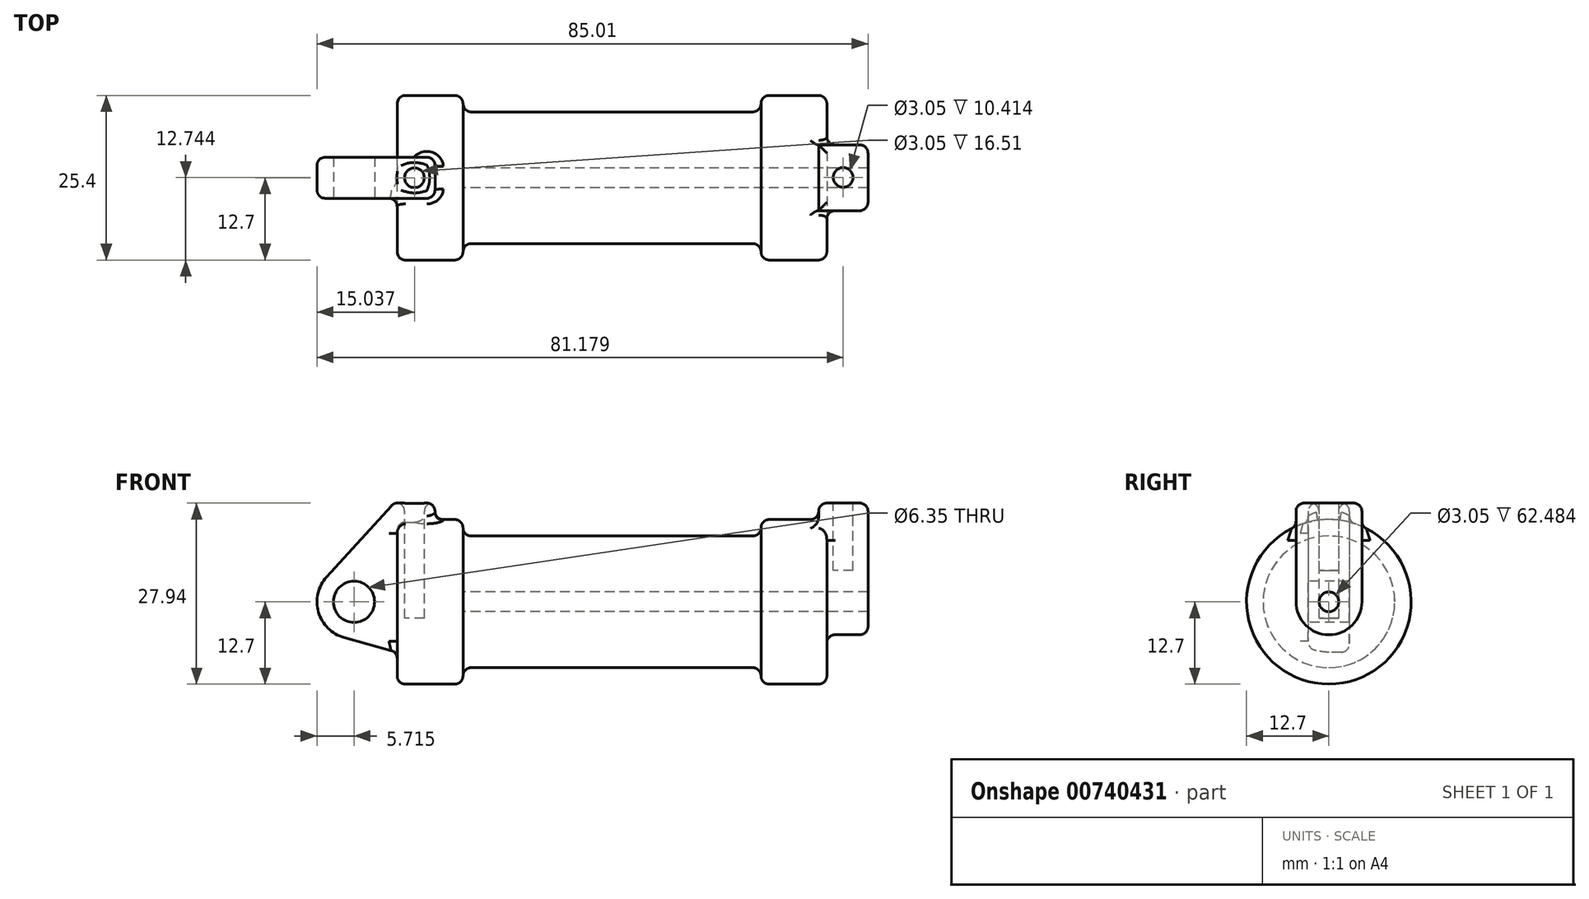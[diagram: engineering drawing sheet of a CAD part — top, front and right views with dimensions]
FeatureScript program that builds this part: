
annotation { "Feature Type Name" : "Feature", "Feature Type Description" : "" }
export const myFeature = defineFeature(function(context is Context, id is Id, definition is map)
    precondition{}
    {
        {
            var Q0;
            Q0=qCreatedBy(makeId("Front.planeOp"),FACE);
            var sketch = newSketch(context, id + "F0", { "sketchPlane" : qUnion([Q0])});
            skLineSegment(sketch, "E0", {"start": v(0, 0) * mm, "end": v(0, 12.7) * mm});
            skLineSegment(sketch, "E1", {"start": v(0, 12.7) * mm, "end": v(10.16, 12.7) * mm});
            skLineSegment(sketch, "E2", {"start": v(10.16, 12.7) * mm, "end": v(10.16, 10.16) * mm});
            skLineSegment(sketch, "E3", {"start": v(10.16, 10.16) * mm, "end": v(56.13, 10.16) * mm});
            skLineSegment(sketch, "E4", {"start": v(56.13, 10.16) * mm, "end": v(56.13, 12.7) * mm});
            skLineSegment(sketch, "E5", {"start": v(56.13, 12.7) * mm, "end": v(66.3, 12.7) * mm});
            skLineSegment(sketch, "E6", {"start": v(66.3, 12.7) * mm, "end": v(66.3, 0) * mm});
            skLineSegment(sketch, "E7", {"start": v(66.3, 0) * mm, "end": v(0, 0) * mm});
            skLineSegment(sketch, "E8", {"start": v(5.84, 15.24) * mm, "end": v(-0.5, 15.24) * mm});
            skLineSegment(sketch, "E9", {"start": v(-0.5, 15.24) * mm, "end": v(-10.88, 3.85) * mm});
            skLineSegment(sketch, "E10", {"start": v(0, 0) * mm, "end": v(-6.65, 0) * mm});
            skCircle(sketch, "E11", {"center": v(-6.65, 0) * mm, "radius": 5.72 * mm});
            skCircle(sketch, "E12", {"center": v(-6.65, 0) * mm, "radius": 3.18 * mm});
            skLineSegment(sketch, "E13", {"start": v(5.84, 15.24) * mm, "end": v(5.84, -9.4) * mm});
            skLineSegment(sketch, "E14", {"start": v(5.84, -9.4) * mm, "end": v(-8.18, -5.5) * mm});
            skSolve(sketch);
        }
        {
            var Q0;
            {var subQ0=sQuery(id+"F0.wireOp",EDGE,"E2");Q0=makeQuery(id+"F0.imprint","IMPRINT",FACE,{"disambiguationData":[TD([[makeQuery(id+"F0.imprint","IMPRINT",EDGE,{"derivedFrom":subQ0}),-1.0]])]});}
            var Q1;
            {var subQ0=sQuery(id+"F0.wireOp",EDGE,"E0");Q1=makeQuery(id+"F0.imprint","IMPRINT",FACE,{"disambiguationData":[TD([[makeQuery(id+"F0.imprint","IMPRINT",EDGE,{"derivedFrom":subQ0}),-1.0]])]});}
            var Q2;
            Q2=sQuery(id+"F0.wireOp",EDGE,"E7");
            revolve(context, id + "F1", {"entities" : qUnion([Q0, Q1]), "axis" : qUnion([Q2]), "revolveType" : RevolveType.FULL});
        }
        {
            var Q0;
            {var subQ1=sQuery(id+"F0.wireOp",EDGE,"E0");Q0=makeQuery(id+"F0.imprint","IMPRINT",FACE,{"disambiguationData":[TD([[makeQuery(id+"F0.imprint","IMPRINT",EDGE,{"derivedFrom":subQ1}),1.0]])]});}
            var Q1;
            {var subQ5=sQuery(id+"F0.wireOp",EDGE,"E12");Q1=makeQuery(id+"F0.imprint","IMPRINT",FACE,{"disambiguationData":[TD([[makeQuery(id+"F0.imprint","IMPRINT",EDGE,{"derivedFrom":subQ5}),-1.0]])]});}
            var Q2;
            {var subQ0=sQuery(id+"F0.wireOp",EDGE,"E14");Q2=makeQuery(id+"F0.imprint","IMPRINT",FACE,{"disambiguationData":[TD([[makeQuery(id+"F0.imprint","IMPRINT",EDGE,{"derivedFrom":subQ0}),-1.0]])]});}
            var Q3;
            {var subQ0=sQuery(id+"F0.wireOp",EDGE,"E0");Q3=makeQuery(id+"F0.imprint","IMPRINT",FACE,{"disambiguationData":[TD([[makeQuery(id+"F0.imprint","IMPRINT",EDGE,{"derivedFrom":subQ0}),-1.0]])]});}
            extrude(context, id + "F2", {"entities" : qUnion([Q0, Q1, Q2, Q3]), "operationType" : NewBodyOperationType.ADD, "oppositeDirection" : true, "depth" : 3.17 * mm, "hasSecondDirection" : true, "secondDirectionOppositeDirection" : false, "secondDirectionDepth" : 3.17 * mm});
        }
        {
            var Q0;
            Q0=makeQuery(id+"F1.opRevolve","SWEPT_FACE",FACE,{"disambiguationData":[OSD([sQuery(id+"F0.wireOp",EDGE,"E6")])]});
            var sketch = newSketch(context, id + "F3", { "sketchPlane" : qUnion([Q0])});
            skCircle(sketch, "E15", {"center": v(0, 0) * mm, "radius": 1.52 * mm});
            skCircle(sketch, "E16", {"center": v(0, 0) * mm, "radius": 5.08 * mm});
            skLineSegment(sketch, "E17", {"start": v(-5.08, 0) * mm, "end": v(-5.08, 15.24) * mm});
            skLineSegment(sketch, "E18", {"start": v(5.08, 0) * mm, "end": v(5.08, 15.24) * mm});
            skLineSegment(sketch, "E19", {"start": v(-5.08, 15.24) * mm, "end": v(5.08, 15.24) * mm});
            skSolve(sketch);
        }
        {
            var Q0;
            Q0=qSketchRegion(id+"F3",true);
            extrude(context, id + "F4", {"entities" : qUnion([Q0]), "operationType" : NewBodyOperationType.ADD, "depth" : 6.35 * mm, "hasSecondDirection" : true, "secondDirectionOppositeDirection" : true, "secondDirectionDepth" : 1.27 * mm});
        }
        {
            var Q0;
            Q0=makeQuery(id+"F3.imprint","IMPRINT",FACE,{"disambiguationData":[TD([[makeQuery(id+"F3.imprint","IMPRINT",EDGE,{"derivedFrom":sQuery(id+"F3.wireOp",EDGE,"E15")}),1.0]])]});
            var Q1;
            Q1=makeQuery(id+"F1.opRevolve","SWEPT_FACE",FACE,{"disambiguationData":[OSD([sQuery(id+"F0.wireOp",EDGE,"E2")])]});
            extrude(context, id + "F5", {"entities" : qUnion([Q0]), "operationType" : NewBodyOperationType.REMOVE, "endBound" : BoundingType.UP_TO_SURFACE, "oppositeDirection" : true, "endBoundEntityFace" : qUnion([Q1]), "depth" : 25.4 * mm});
        }
        {
            var Q0;
            Q0=makeQuery(id+"F4.opExtrude","SWEPT_FACE",FACE,{"disambiguationData":[OSD([sQuery(id+"F3.wireOp",EDGE,"E19")])]});
            var sketch = newSketch(context, id + "F6", { "sketchPlane" : qUnion([Q0])});
            skCircle(sketch, "E20", {"center": v(68.8, 0.04) * mm, "radius": 1.52 * mm});
            skSolve(sketch);
        }
        {
            var Q0;
            Q0=makeQuery(id+"F2.opExtrude","SWEPT_FACE",FACE,{"disambiguationData":[OSD([sQuery(id+"F0.wireOp",EDGE,"E8")])]});
            var sketch = newSketch(context, id + "F7", { "sketchPlane" : qUnion([Q0])});
            skCircle(sketch, "E21", {"center": v(2.67, 0) * mm, "radius": 1.52 * mm});
            skPoint(sketch, "E21.centerSnap0", {"position": v(5.84, 0) * mm});
            skSolve(sketch);
        }
        {
            var Q0;
            Q0=qSketchRegion(id+"F6",true);
            extrude(context, id + "F8", {"entities" : qUnion([Q0]), "operationType" : NewBodyOperationType.REMOVE, "oppositeDirection" : true, "depth" : 10.4 * mm});
        }
        {
            var Q0;
            Q0=qSketchRegion(id+"F7",true);
            extrude(context, id + "F9", {"entities" : qUnion([Q0]), "operationType" : NewBodyOperationType.REMOVE, "oppositeDirection" : true, "depth" : 17.78 * mm});
        }
        {
            var Q0;
            Q0=makeQuery(id+"F1.opRevolve","SWEPT_EDGE",EDGE,{"disambiguationData":[OSD([sQuery(id+"F0.wireOp",EDGE,"E1"),sQuery(id+"F0.wireOp",EDGE,"E2")])]});
            var Q1;
            Q1=makeQuery(id+"F1.opRevolve","SWEPT_EDGE",EDGE,{"disambiguationData":[OSD([sQuery(id+"F0.wireOp",EDGE,"E2"),sQuery(id+"F0.wireOp",EDGE,"E3")])]});
            var Q2;
            Q2=makeQuery(id+"F1.opRevolve","SWEPT_EDGE",EDGE,{"disambiguationData":[OSD([sQuery(id+"F0.wireOp",EDGE,"E4"),sQuery(id+"F0.wireOp",EDGE,"E5")])]});
            var Q3;
            Q3=makeQuery(id+"F1.opRevolve","SWEPT_EDGE",EDGE,{"disambiguationData":[OSD([sQuery(id+"F0.wireOp",EDGE,"E3"),sQuery(id+"F0.wireOp",EDGE,"E4")])]});
            var Q4;
            Q4=makeQuery(id+"F1.opRevolve","SWEPT_EDGE",EDGE,{"disambiguationData":[OSD([sQuery(id+"F0.wireOp",EDGE,"E5"),sQuery(id+"F0.wireOp",EDGE,"E6")])]});
            var Q5;
            Q5=makeQuery(id+"F1.opRevolve","SWEPT_EDGE",EDGE,{"disambiguationData":[OSD([sQuery(id+"F0.wireOp",EDGE,"E0"),sQuery(id+"F0.wireOp",EDGE,"E1")])]});
            fillet(context, id + "F10", {"entities" : qUnion([Q0, Q1, Q2, Q3, Q4, Q5]), "radius" : 1.27 * mm, "tangentPropagation" : true, "allowEdgeOverflow" : false});
        }
        {
            var Q0;
            Q0=makeQuery(id+"F4.opExtrude","CAP_EDGE",EDGE,{"disambiguationData":[OSD([sQuery(id+"F3.wireOp",EDGE,"E18")])],"isStart":false});
            var Q1;
            Q1=makeQuery(id+"F4.boolean.opBoolean","INTERSECT",EDGE,{"derivedFrom":[makeQuery(id+"F1.opRevolve","SWEPT_FACE",FACE,{"disambiguationData":[OSD([sQuery(id+"F0.wireOp",EDGE,"E6")])]}),makeQuery(id+"F4.opExtrude","SWEPT_FACE",FACE,{"disambiguationData":[OSD([sQuery(id+"F3.wireOp",EDGE,"E18")])]})]});
            var Q2;
            Q2=makeQuery(id+"F4.boolean.opBoolean","INTERSECT",EDGE,{"derivedFrom":[makeQuery(id+"F1.opRevolve","SWEPT_FACE",FACE,{"disambiguationData":[OSD([sQuery(id+"F0.wireOp",EDGE,"E5")])]}),makeQuery(id+"F4.opExtrude","CAP_FACE",FACE,{"disambiguationData":[OSD([sQuery(id+"F3.wireOp",EDGE,"E15"),sQuery(id+"F3.wireOp",EDGE,"E16"),sQuery(id+"F3.wireOp",EDGE,"E17"),sQuery(id+"F3.wireOp",EDGE,"E18"),sQuery(id+"F3.wireOp",EDGE,"E19")])],"isStart":true})]});
            var Q3;
            Q3=makeQuery(id+"F4.opExtrude","CAP_EDGE",EDGE,{"disambiguationData":[OSD([sQuery(id+"F3.wireOp",EDGE,"E19")])],"isStart":true});
            var Q4;
            Q4=makeQuery(id+"F4.opExtrude","SWEPT_EDGE",EDGE,{"disambiguationData":[OSD([sQuery(id+"F3.wireOp",EDGE,"E18"),sQuery(id+"F3.wireOp",EDGE,"E19")])]});
            var Q5;
            Q5=makeQuery(id+"F4.opExtrude","CAP_EDGE",EDGE,{"disambiguationData":[OSD([sQuery(id+"F3.wireOp",EDGE,"E19")])],"isStart":false});
            var Q6;
            Q6=makeQuery(id+"F4.opExtrude","SWEPT_EDGE",EDGE,{"disambiguationData":[OSD([sQuery(id+"F3.wireOp",EDGE,"E17"),sQuery(id+"F3.wireOp",EDGE,"E19")])]});
            fillet(context, id + "F11", {"entities" : qUnion([Q0, Q1, Q2, Q3, Q4, Q5, Q6]), "radius" : 1.27 * mm, "tangentPropagation" : true, "allowEdgeOverflow" : false});
        }
        {
            var Q0;
            Q0=makeQuery(id+"F2.boolean.opBoolean","INTERSECT",EDGE,{"derivedFrom":[makeQuery(id+"F1.opRevolve","SWEPT_FACE",FACE,{"disambiguationData":[OSD([sQuery(id+"F0.wireOp",EDGE,"E0")])]}),makeQuery(id+"F2.opExtrude","CAP_FACE",FACE,{"disambiguationData":[OSD([sQuery(id+"F0.wireOp",EDGE,"E8"),sQuery(id+"F0.wireOp",EDGE,"E9"),sQuery(id+"F0.wireOp",EDGE,"E11"),sQuery(id+"F0.wireOp",EDGE,"E12"),sQuery(id+"F0.wireOp",EDGE,"E13"),sQuery(id+"F0.wireOp",EDGE,"E14")])],"isStart":true})]});
            var Q1;
            Q1=makeQuery(id+"F2.opExtrude","CAP_EDGE",EDGE,{"disambiguationData":[OSD([sQuery(id+"F0.wireOp",EDGE,"E9")])],"isStart":true});
            var Q2;
            Q2=makeQuery(id+"F2.opExtrude","CAP_EDGE",EDGE,{"disambiguationData":[OSD([sQuery(id+"F0.wireOp",EDGE,"E11")])],"isStart":true});
            var Q3;
            Q3=makeQuery(id+"F2.opExtrude","CAP_EDGE",EDGE,{"disambiguationData":[OSD([sQuery(id+"F0.wireOp",EDGE,"E11")])],"isStart":false});
            var Q4;
            Q4=makeQuery(id+"F2.opExtrude","SWEPT_EDGE",EDGE,{"disambiguationData":[OSD([sQuery(id+"F0.wireOp",EDGE,"E8"),sQuery(id+"F0.wireOp",EDGE,"E13")])]});
            var Q5;
            Q5=makeQuery(id+"F2.opExtrude","CAP_EDGE",EDGE,{"disambiguationData":[OSD([sQuery(id+"F0.wireOp",EDGE,"E8")])],"isStart":false});
            var Q6;
            Q6=makeQuery(id+"F2.opExtrude","SWEPT_FACE",FACE,{"disambiguationData":[OSD([sQuery(id+"F0.wireOp",EDGE,"E8")])]});
            var Q7;
            Q7=makeQuery(id+"F2.boolean.opBoolean","INTERSECT",EDGE,{"derivedFrom":[makeQuery(id+"F1.opRevolve","SWEPT_FACE",FACE,{"disambiguationData":[OSD([sQuery(id+"F0.wireOp",EDGE,"E1")])]}),makeQuery(id+"F2.opExtrude","SWEPT_FACE",FACE,{"disambiguationData":[OSD([sQuery(id+"F0.wireOp",EDGE,"E13")])]})]});
            var Q8;
            Q8=makeQuery(id+"F2.opExtrude","CAP_EDGE",EDGE,{"disambiguationData":[OSD([sQuery(id+"F0.wireOp",EDGE,"E13")])],"isStart":false});
            var Q9;
            Q9=makeQuery(id+"F2.opExtrude","CAP_EDGE",EDGE,{"disambiguationData":[OSD([sQuery(id+"F0.wireOp",EDGE,"E13")])],"isStart":true});
            fillet(context, id + "F12", {"entities" : qUnion([Q0, Q1, Q2, Q3, Q4, Q5, Q6, Q7, Q8, Q9]), "radius" : 1.27 * mm, "tangentPropagation" : true, "allowEdgeOverflow" : false});
        }
    });
